# Revit family: Speaker-Ceiling-TOA-F-1522 clean
name_source: partatom
category: Communication Devices
revit_build: Autodesk Revit 2013 (Build: 20130531_2115(x64)
units: mm (PartAtom-declared; Revit-internal decimal feet)

## types (1)
- 4"
    100V Taps = 6W & 3W
    25V Taps = 0.75W, 0.4 W & 0.2 W
    70V Taps = 6W, 3W & 1.5W
    Assembly Code = E1020300
    Bag Material = Fabric - TOA - Black
    Body Diameter = 5.315 "
    Body Radius = 2.658 "
    Coverage Horizontal = 160.00°
    Coverage Vertical = 160.00°
    Default Elevation = 48 "
    Description = COMPACT FULL-RANGE CEILING SPEAKER (4”)
    Grille Diameter = 6.102 "
    Grille Height = 0.433 "
    Grille Material = Mesh - TOA - White
    Grille Radius = 3.051 "
    Height = 4.606 "
    Highlight Material = Paint - TOA - White
    IQ Category = Speaker
    Length 1 = 2.933 "
    Load Classification = Other
    Long Term Power Handling = 18 W
    Manufacturer = TOA Electronics Inc.
    Manufacturer URL = http://www.toaelectronics.com
    Maximum Ceiling Thickness = 1.457 "
    Model = F-1522SC
    Mounting Options = Ceiling Reinforcement Ring
    Offset = 0 "
    Operating Weight = 2.20 lb
    Product Documentation Link = http://www.toaelectronics.com
    Product Name = F-1522SC
    Product Page URL = http://www.toaelectronics.com
    Regulatory Compliance = UL
    SPL Measurement Bandwidth = 65 to 18k Hz
    Sensitivity = 88
    Transformer Option = Yes
    Type Comments = F-1522SC
    URL = http://www.toaelectronics.com
    Weight Product = 2.2
    Width = 6.102 "

## geometry (parser evidence)
native form markers: Blend x10, Sweep x5
no freeform markers — native parametric forms only
